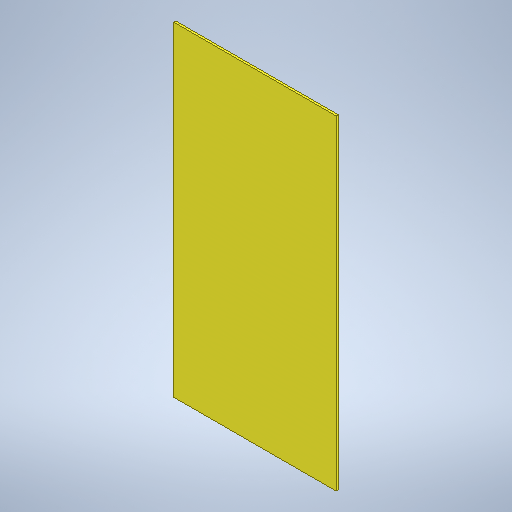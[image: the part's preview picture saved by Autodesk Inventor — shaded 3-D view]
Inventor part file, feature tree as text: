
AUTODESK INVENTOR PART (.ipt)
format: ipt  version: 2025 (Build 290162010, 162A)  size: 244,224 bytes
history: native  units: in
note: dims shown in document units (in); Inventor stores cm internally (conversion verified against a paired STEP export)
features: extrude x1, sketch x1
ambient origin geometry x8: Origin, YZ Plane, XZ Plane, XY Plane, X Axis, Y Axis, Z Axis, Center Point
bodies: Solid1 (feature_tree)
feature tree (2):
  extrude  "Extrusion1"  Depth=48.0in
  sketch  "Sketch1"  dims[d2=96.0in d3=48.0in d4=0.625in d5=0.0in]
